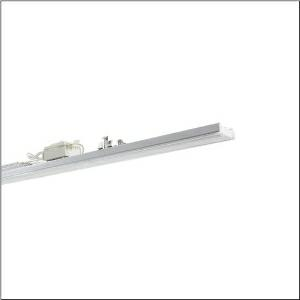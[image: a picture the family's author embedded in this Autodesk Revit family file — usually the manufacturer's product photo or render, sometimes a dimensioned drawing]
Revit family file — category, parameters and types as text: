
# Revit family: licross_21_recessed_ho_52tl12dv4l2m
name_source: partatom
category: Lighting Fixtures
units: mm (PartAtom-declared; Revit-internal decimal feet)

## family parameters
Cut with Voids When Loaded = No
Host = Face
Light Source = No
Part Type = Normal
Room Calculation Point = No
Round Connector Dimension = Use Diameter
Shared = No

## types (1)
- --- (1 x LED, 22710 lm, 125.6 W, 4000K)
    Apparent Load = 126 VA
    CIE Flux Codes = 69 91 98 100 100
    Color Rendering = 80
    Color Temperature = 4000K
    Default Elevation = 1800 mm
    Description = Licross 21 Recessed HO, luminaire insert, of sheet steel, galvanised, coil coated, white, length: 2.250mm, width: 66mm, height: 67mm, LED rated luminous flux: 22.710lm, light colour: 840, SDCM (Standard Deviation of Colour Matching)MacAdam ≤ 3 SDCM (initial), control gear: DALI 2, with plug, 5-pole, with phase selection, mains connection: 220..240V, AC, 50/60Hz, rated input power: 126W, internal wiring halogen-free, primary optical cover: cover, of PMMA, light emission: direct distribution, primary light characteristic: symmetric, protection rating (complete): IP40, insulation class (complete): insulation class I (protective earthing), certification: CE, ENEC, VDE, UKCA, protection symbol: D if used in an environment without relevant dust loads with corresponding accessories, impact resistance: IK06, permissible ambient temperature for indoor applications: -40..+30°C, corresponds to IFS (International Featured Standards) requirements for safety and quality in the food industry, reducing of maximum allowable ambient temperature of 5°C with ceiling mounting, LABS conformity tested according to VDMA 24364:2018-05, The light source and the operating device comply with the requirements of the Ecodesign Regulation (EU) 2019/2020 and are replaceable in accordance with this regulation, packaging unit: 1 piece
    Height = 58 mm
    Lamp = 1 x LED
    Lamp Light Flux = 22710 lm
    Lamp Power = 125.6 W
    Lamp count = 1
    Length = 2250 mm
    Luminous efficacy = 181 lm/W
    Manufacturer = Siteco
    ModVariant = No
    Model = 52TL12DV4L2M
    Mounting Place = Ceiling
    Mounting Type = Pendant
    Number of Poles = 1
    OnlyDefault = Yes
    Power Factor = 1
    Product Name = Licross 21 Recessed HO
    Product group = luminaire insert | ceiling pendant
    ProductGroupID = 901
    Protection Class = Protection class I
    Protection Degree = IP 40
    RLX_Detail_Level = 1
    RLX_Emergency_Light_Flux = 0 lm
    RLX_Emergency_Type = 0
    RLX_Emergency_Type_DB = No
    RlxData = <blob elided: 29833 chars, md5=920e6d0d>
    Socket = socket
    Standby Power = 0 W
    System Light Flux = 22710 lm
    System Power = 126 W
    Type Comments = factory setting: luminous flux: 100 % | dim-lin: 254 | 489 mA
    Type Image = l_1296930.jpg
    URL = http://relux.com
    VarID = @adj_116893
    Voltage = 0 V
    Weight = 0.00 kg
    Width = 66 mm

## geometry (parser evidence)
native form markers: Blend x4, Sweep x10
no freeform markers — native parametric forms only
